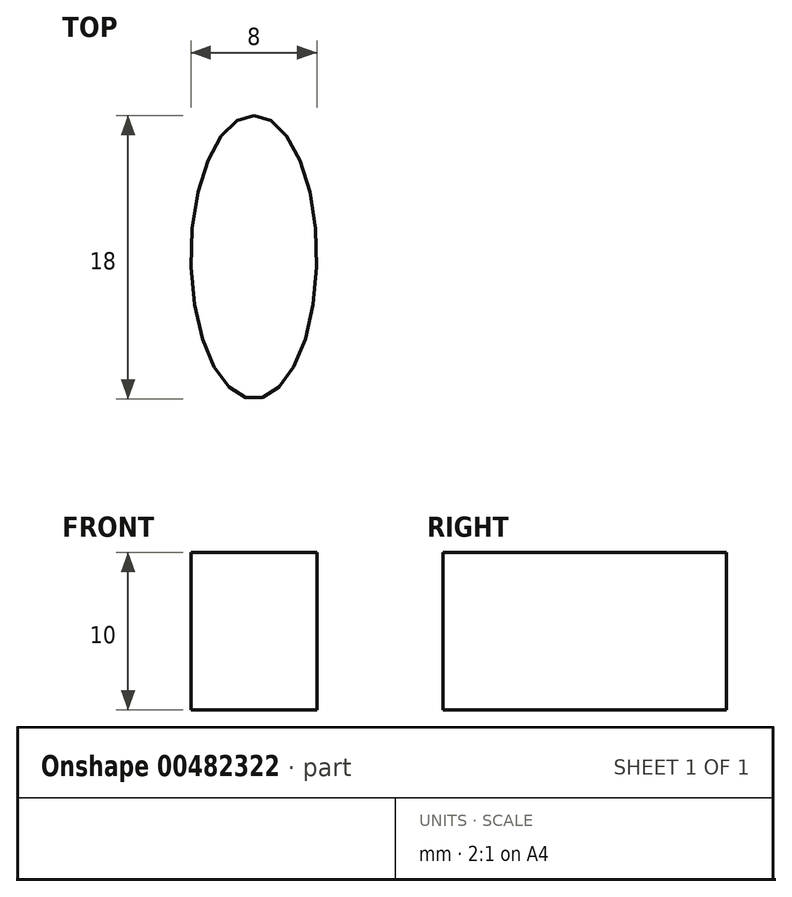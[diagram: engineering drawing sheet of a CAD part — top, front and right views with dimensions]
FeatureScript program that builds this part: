
annotation { "Feature Type Name" : "Feature", "Feature Type Description" : "" }
export const myFeature = defineFeature(function(context is Context, id is Id, definition is map)
    precondition{}
    {
        {
            var Q0;
            Q0=qCreatedBy(makeId("Top.planeOp"),FACE);
            var sketch = newSketch(context, id + "F0", { "sketchPlane" : qUnion([Q0])});
            skEllipse(sketch, "E0", {"center": v(0, -1.97) * mm, "majorRadius": 9 * mm, "minorRadius": 4 * mm, "majorAxis": v(0, 1)});
            skSolve(sketch);
        }
        {
            var Q0;
            Q0 = qConstructionFilter(qBodyType(qCreatedBy(id + "F0" ,EDGE), BodyType.WIRE), ConstructionObject.NO);
            extrude(context, id + "F1", {"bodyType" : ToolBodyType.SURFACE, "surfaceEntities" : qUnion([Q0]), "depth" : 10 * mm, "offsetDistance" : 25 * mm});
        }
    });
